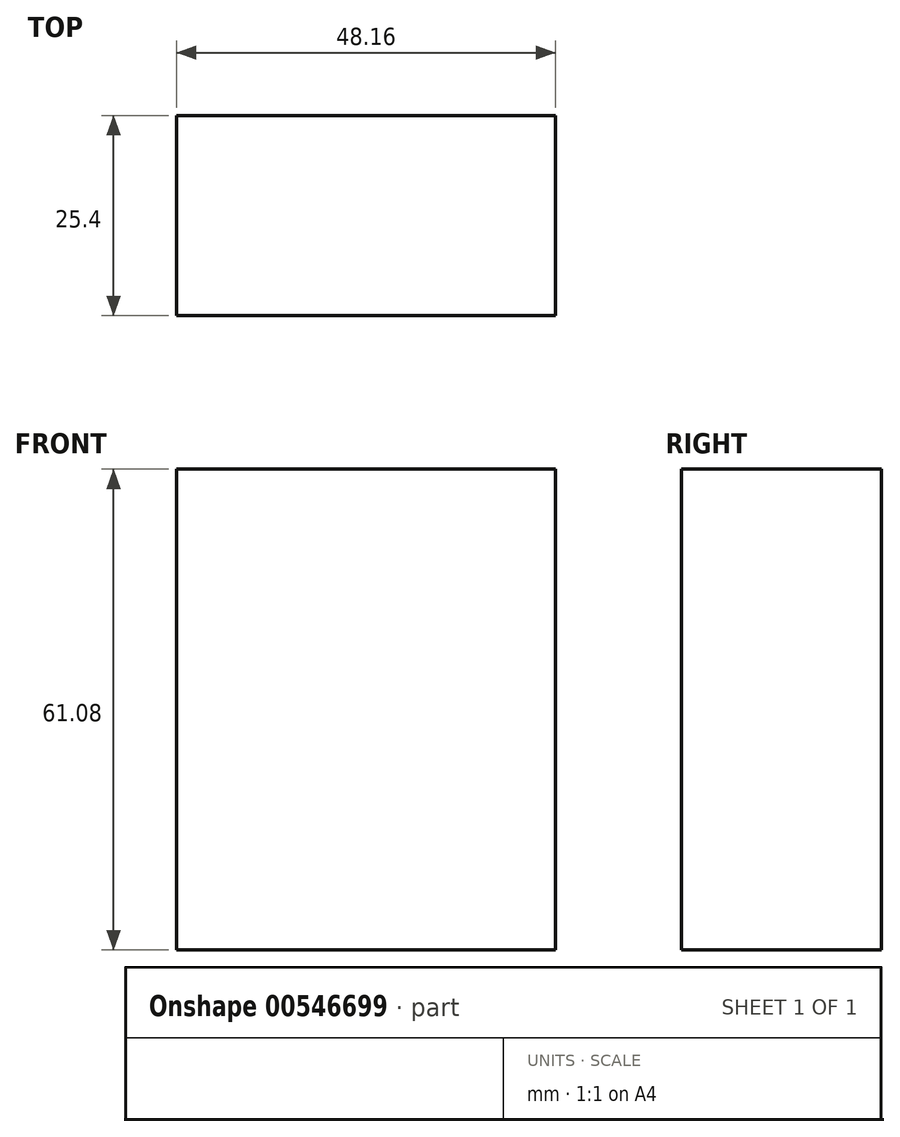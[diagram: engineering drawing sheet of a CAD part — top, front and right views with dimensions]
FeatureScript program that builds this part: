
annotation { "Feature Type Name" : "Feature", "Feature Type Description" : "" }
export const myFeature = defineFeature(function(context is Context, id is Id, definition is map)
    precondition{}
    {
        {
            var Q0;
            Q0=qCreatedBy(makeId("Front.planeOp"),FACE);
            var sketch = newSketch(context, id + "F0", { "sketchPlane" : qUnion([Q0])});
            skLineSegment(sketch, "E0.bottom", {"start": v(-117.35, 50.4) * mm, "end": v(-69.2, 50.4) * mm});
            skLineSegment(sketch, "E0.top", {"start": v(-117.35, -10.68) * mm, "end": v(-69.2, -10.68) * mm});
            skLineSegment(sketch, "E0.left", {"start": v(-117.35, 50.4) * mm, "end": v(-117.35, -10.68) * mm});
            skLineSegment(sketch, "E0.right", {"start": v(-69.2, 50.4) * mm, "end": v(-69.2, -10.68) * mm});
            skSolve(sketch);
        }
        {
            var Q0;
            Q0=qSketchRegion(id+"F0",true);
            extrude(context, id + "F1", {"entities" : qUnion([Q0]), "depth" : 25.4 * mm, "offsetDistance" : 25.4 * mm});
        }
    });
